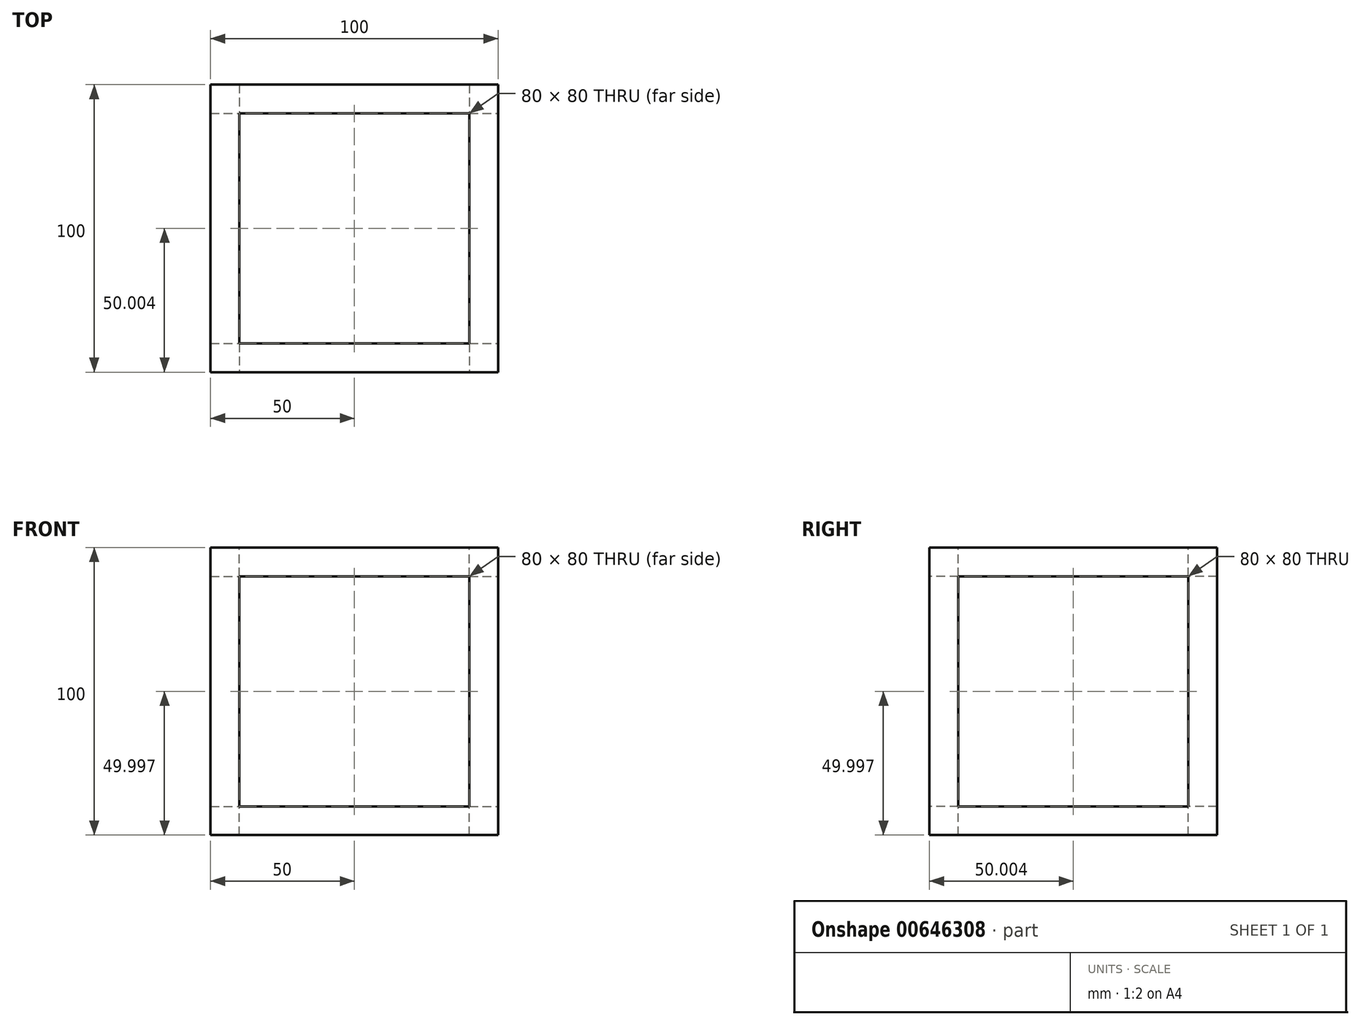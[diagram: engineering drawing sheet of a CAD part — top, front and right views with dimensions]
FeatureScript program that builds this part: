
annotation { "Feature Type Name" : "Feature", "Feature Type Description" : "" }
export const myFeature = defineFeature(function(context is Context, id is Id, definition is map)
    precondition{}
    {
        {
            var Q0;
            Q0=qCreatedBy(makeId("Right.planeOp"),FACE);
            var sketch = newSketch(context, id + "F0", { "sketchPlane" : qUnion([Q0])});
            skLineSegment(sketch, "E0.bottom", {"start": v(-46.74, 53.23) * mm, "end": v(53.26, 53.23) * mm});
            skLineSegment(sketch, "E0.top", {"start": v(-46.74, -46.77) * mm, "end": v(53.26, -46.77) * mm});
            skLineSegment(sketch, "E0.left", {"start": v(-46.74, 53.23) * mm, "end": v(-46.74, -46.77) * mm});
            skLineSegment(sketch, "E0.right", {"start": v(53.26, 53.23) * mm, "end": v(53.26, -46.77) * mm});
            skSolve(sketch);
        }
        {
            var Q0;
            Q0=makeQuery(id+"F0.imprint","IMPRINT",FACE,{"disambiguationData":[TD([[makeQuery(id+"F0.imprint","IMPRINT",EDGE,{"derivedFrom":sQuery(id+"F0.wireOp",EDGE,"E0.bottom")}),-1.0]])]});
            extrude(context, id + "F1", {"entities" : qUnion([Q0]), "endBound" : BoundingType.SYMMETRIC, "depth" : 100 * mm, "offsetDistance" : 25 * mm});
        }
        {
            var Q0;
            Q0=makeQuery(id+"F1.opExtrude","SWEPT_FACE",FACE,{"disambiguationData":[OSD([sQuery(id+"F0.wireOp",EDGE,"E0.left")])]});
            var sketch = newSketch(context, id + "F2", { "sketchPlane" : qUnion([Q0])});
            skLineSegment(sketch, "E1.bottom", {"start": v(-40, 43.23) * mm, "end": v(40, 43.23) * mm});
            skLineSegment(sketch, "E1.top", {"start": v(-40, -36.77) * mm, "end": v(40, -36.77) * mm});
            skLineSegment(sketch, "E1.left", {"start": v(-40, 43.23) * mm, "end": v(-40, -36.77) * mm});
            skLineSegment(sketch, "E1.right", {"start": v(40, 43.23) * mm, "end": v(40, -36.77) * mm});
            skSolve(sketch);
        }
        {
            var Q0;
            Q0=makeQuery(id+"F2.imprint","IMPRINT",FACE,{"disambiguationData":[TD([[makeQuery(id+"F2.imprint","IMPRINT",EDGE,{"derivedFrom":sQuery(id+"F2.wireOp",EDGE,"E1.bottom")}),-1.0]])]});
            extrude(context, id + "F3", {"entities" : qUnion([Q0]), "operationType" : NewBodyOperationType.REMOVE, "oppositeDirection" : true, "depth" : 100 * mm, "offsetDistance" : 25 * mm});
        }
        {
            var Q0;
            Q0=makeQuery(id+"F1.opExtrude","SWEPT_FACE",FACE,{"disambiguationData":[OSD([sQuery(id+"F0.wireOp",EDGE,"E0.bottom")])]});
            var sketch = newSketch(context, id + "F4", { "sketchPlane" : qUnion([Q0])});
            skLineSegment(sketch, "E2.bottom", {"start": v(-40, 43.26) * mm, "end": v(40, 43.26) * mm});
            skLineSegment(sketch, "E2.top", {"start": v(-40, -36.74) * mm, "end": v(40, -36.74) * mm});
            skLineSegment(sketch, "E2.left", {"start": v(-40, 43.26) * mm, "end": v(-40, -36.74) * mm});
            skLineSegment(sketch, "E2.right", {"start": v(40, 43.26) * mm, "end": v(40, -36.74) * mm});
            skSolve(sketch);
        }
        {
            var Q0;
            Q0=makeQuery(id+"F4.imprint","IMPRINT",FACE,{"disambiguationData":[TD([[makeQuery(id+"F4.imprint","IMPRINT",EDGE,{"derivedFrom":sQuery(id+"F4.wireOp",EDGE,"E2.bottom")}),-1.0]])]});
            extrude(context, id + "F5", {"entities" : qUnion([Q0]), "operationType" : NewBodyOperationType.REMOVE, "oppositeDirection" : true, "depth" : 100 * mm, "offsetDistance" : 25 * mm});
        }
        {
            var Q0;
            Q0=makeQuery(id+"F1.opExtrude","CAP_FACE",FACE,{"disambiguationData":[OSD([sQuery(id+"F0.wireOp",EDGE,"E0.bottom"),sQuery(id+"F0.wireOp",EDGE,"E0.top"),sQuery(id+"F0.wireOp",EDGE,"E0.left"),sQuery(id+"F0.wireOp",EDGE,"E0.right")])],"isStart":false});
            var sketch = newSketch(context, id + "F6", { "sketchPlane" : qUnion([Q0])});
            skLineSegment(sketch, "E3.bottom", {"start": v(-36.74, 43.23) * mm, "end": v(43.26, 43.23) * mm});
            skLineSegment(sketch, "E3.top", {"start": v(-36.74, -36.77) * mm, "end": v(43.26, -36.77) * mm});
            skLineSegment(sketch, "E3.left", {"start": v(-36.74, 43.23) * mm, "end": v(-36.74, -36.77) * mm});
            skLineSegment(sketch, "E3.right", {"start": v(43.26, 43.23) * mm, "end": v(43.26, -36.77) * mm});
            skSolve(sketch);
        }
        {
            var Q0;
            Q0=makeQuery(id+"F6.imprint","IMPRINT",FACE,{"disambiguationData":[TD([[makeQuery(id+"F6.imprint","IMPRINT",EDGE,{"derivedFrom":sQuery(id+"F6.wireOp",EDGE,"E3.bottom")}),-1.0]])]});
            extrude(context, id + "F7", {"entities" : qUnion([Q0]), "operationType" : NewBodyOperationType.REMOVE, "oppositeDirection" : true, "depth" : 100 * mm, "offsetDistance" : 25 * mm});
        }
    });
